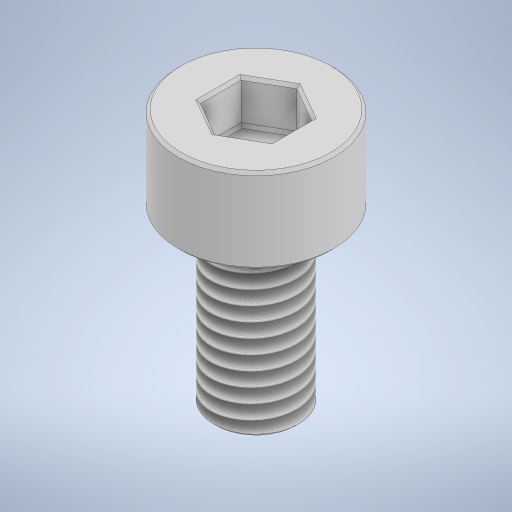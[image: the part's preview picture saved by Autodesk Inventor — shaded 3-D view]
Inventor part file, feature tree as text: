
AUTODESK INVENTOR PART (.ipt)
format: ipt  version: 2023 (Build 270158000, 158)  size: 303,104 bytes
history: native  units: in
note: dims shown in document units (in); Inventor stores cm internally (conversion verified against a paired STEP export)
features: sketch x2, revolve x1, thread x1, extrude x1, chamfer x1
ambient origin geometry x8: Origin, YZ Plane, XZ Plane, XY Plane, X Axis, Y Axis, Z Axis, Center Point
bodies: Solid1 (feature_tree)
feature tree (6):
  revolve  "Revolution1"  [1 undecoded]
  thread  "Thread1"  [1 undecoded]
  extrude  "Extrusion2"  TaperAngle=90.0deg  [1 undecoded]
  chamfer  "Chamfer2"  Distance=0.1181in
  sketch  "Sketch1"  dims[d0=0.1083in d1=0.1181in d2=0.2362in]
  sketch  "Sketch3"  dims[d3=0.0591in d4=90.0deg d5=0.1181in d6=0.0in d13=0.0984in d14=0.0591in d15=0.0in d16=0.0039in d17=0.0787in d18=45.0deg]
note: 3 required parameter values undecoded (feature->parameter linkage not recoverable at this tier; creation-order binding heuristic only, values carry confidence <= 0.55)